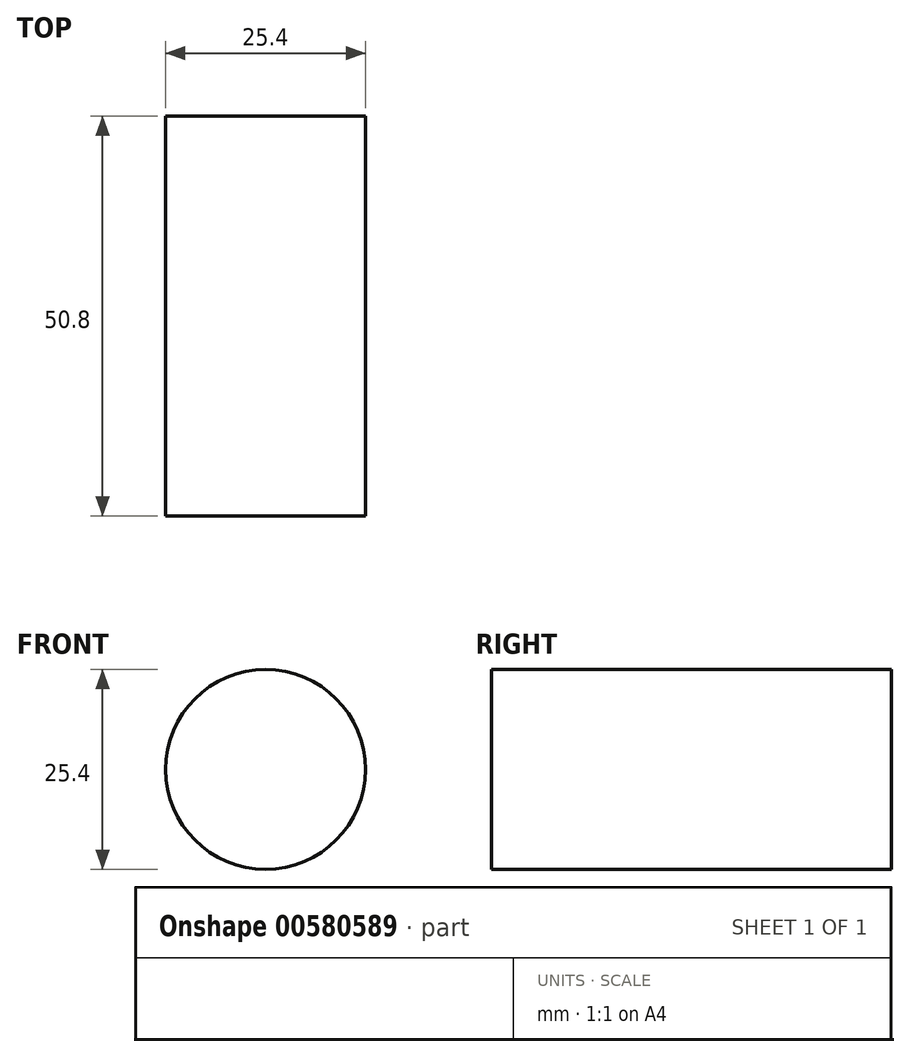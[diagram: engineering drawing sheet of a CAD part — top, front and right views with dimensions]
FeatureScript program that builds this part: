
annotation { "Feature Type Name" : "Feature", "Feature Type Description" : "" }
export const myFeature = defineFeature(function(context is Context, id is Id, definition is map)
    precondition{}
    {
        {
            var Q0;
            Q0=qCreatedBy(makeId("Front.planeOp"),FACE);
            var sketch = newSketch(context, id + "F0", { "sketchPlane" : qUnion([Q0])});
            skCircle(sketch, "E0", {"center": v(0, 0) * mm, "radius": 12.7 * mm});
            skSolve(sketch);
        }
        {
            var Q0;
            Q0=makeQuery(id+"F0.imprint","IMPRINT",FACE,{"disambiguationData":[TD([[makeQuery(id+"F0.imprint","IMPRINT",EDGE,{"derivedFrom":sQuery(id+"F0.wireOp",EDGE,"E0")}),1.0]])]});
            extrude(context, id + "F1", {"entities" : qUnion([Q0]), "depth" : 50.8 * mm, "offsetDistance" : 25.4 * mm});
        }
    });
